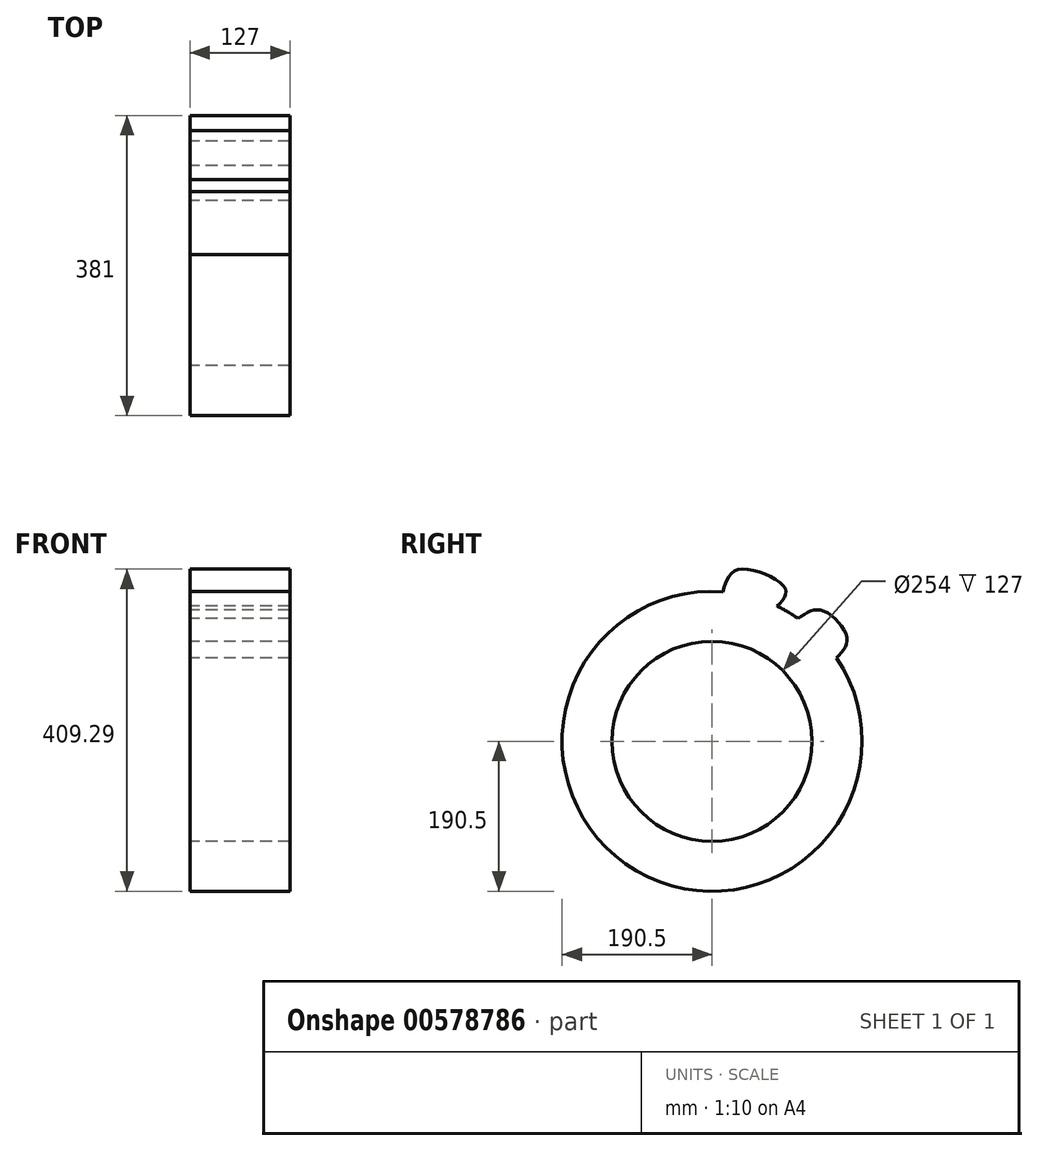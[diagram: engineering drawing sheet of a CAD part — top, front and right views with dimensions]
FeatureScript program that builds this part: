
annotation { "Feature Type Name" : "Feature", "Feature Type Description" : "" }
export const myFeature = defineFeature(function(context is Context, id is Id, definition is map)
    precondition{}
    {
        {
            var Q0;
            Q0=qCreatedBy(makeId("Right.planeOp"),FACE);
            var sketch = newSketch(context, id + "F0", { "sketchPlane" : qUnion([Q0])});
            skArc(sketch, "E0", {"start": v(109.31, 156.02) * mm, "mid": v(96.23, 164.4) * mm, "end": v(82.51, 171.7) * mm});
            skCircle(sketch, "E1", {"center": v(0, 0) * mm, "radius": 127 * mm});
            skFitSpline(sketch, "E2", {"points": [v(158.26, 106.03) * mm, v(171.19, 131.7) * mm, v(138.97, 166.44) * mm, v(109.31, 156.02) * mm], "startDerivative": vector(72.77, 76.46) * mm, "endDerivative": vector(-88.46, -63.54) * mm});
            skFitSpline(sketch, "E3", {"points": [v(82.51, 171.7) * mm, v(92.87, 194.23) * mm, v(34.13, 218.23) * mm, v(13.87, 190) * mm], "startDerivative": vector(81.45, 82.57) * mm, "endDerivative": vector(-34.59, -122.87) * mm});
            skArc(sketch, "E4.trimOffspring", {"start": v(13.87, 190) * mm, "mid": v(-95.76, -164.68) * mm, "end": v(158.26, 106.03) * mm});
            skSolve(sketch);
        }
        {
            var Q0;
            Q0=makeQuery(id+"F0.imprint","IMPRINT",FACE,{"disambiguationData":[TD([[makeQuery(id+"F0.imprint","IMPRINT",EDGE,{"derivedFrom":sQuery(id+"F0.wireOp",EDGE,"E0")}),1.0]])]});
            extrude(context, id + "F1", {"entities" : qUnion([Q0]), "depth" : 127 * mm, "offsetDistance" : 25.4 * mm});
        }
    });
